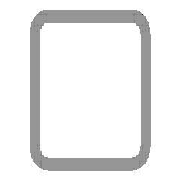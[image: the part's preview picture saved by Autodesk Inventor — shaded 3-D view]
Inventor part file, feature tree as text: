
AUTODESK INVENTOR PART (.ipt)
format: ipt  version: 2025.1 (Build 291241020, 241B)  size: 145,408 bytes
history: native  units: mm (DEFAULTED — no unit token found)
features: other x4, sketch x1, plane x1
ambient origin geometry x8: Origin, YZ Plane, XZ Plane, XY Plane, X Axis, Y Axis, Z Axis, Center Point
bodies: Solid1 (feature_tree), Body (feature_tree)
feature tree (6):
  parser-record x1  (decoder bookkeeping rows leaked as tree rows — omitted from the tree; the rows remain in map.json)
  other  "Driven Length"
  other  "Start plane"
  other  "End plane"
  sketch  "Sketch3"  dims[d3=1250.0mm d4=0.0mm d7=6.0mm d9=100.0mm d11=100.0mm d12=3.0mm d13=50.0mm d14=1300.0mm d15=50.0mm d16=50.0mm d17=90.0deg d18=1250.0mm]
  plane  "Work Plane3"
